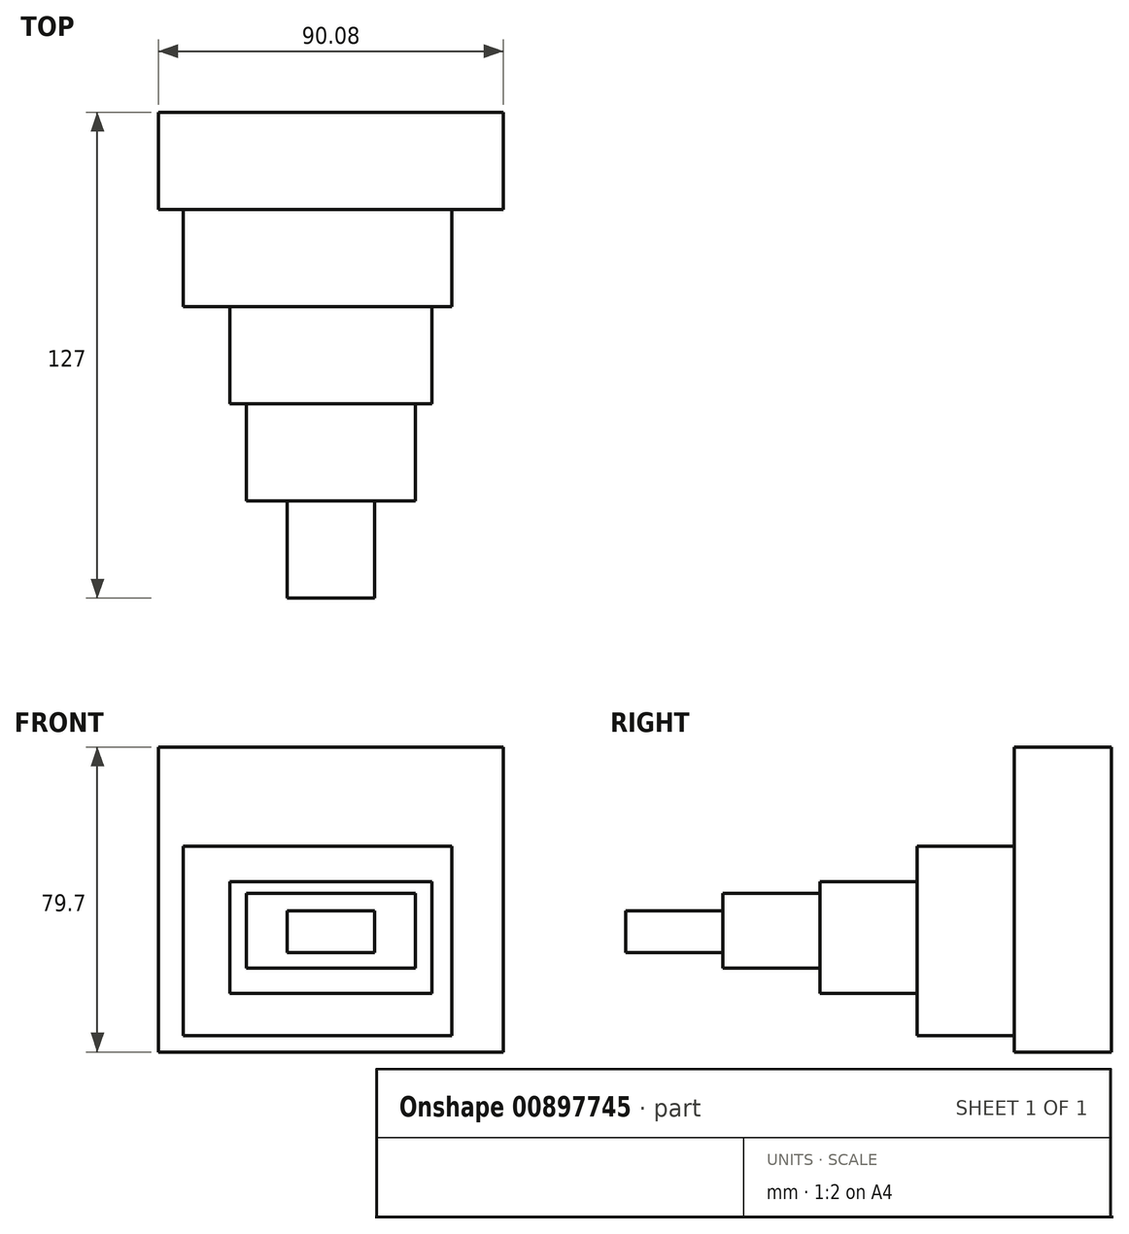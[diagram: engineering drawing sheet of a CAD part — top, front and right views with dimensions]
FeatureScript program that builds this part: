
annotation { "Feature Type Name" : "Feature", "Feature Type Description" : "" }
export const myFeature = defineFeature(function(context is Context, id is Id, definition is map)
    precondition{}
    {
        {
            var Q0;
            Q0=qCreatedBy(makeId("Front.planeOp"),FACE);
            var sketch = newSketch(context, id + "F0", { "sketchPlane" : qUnion([Q0])});
            skLineSegment(sketch, "E0.bottom", {"start": v(45.04, -39.85) * mm, "end": v(-45.04, -39.85) * mm});
            skLineSegment(sketch, "E0.top", {"start": v(45.04, 39.85) * mm, "end": v(-45.04, 39.85) * mm});
            skLineSegment(sketch, "E0.left", {"start": v(45.04, -39.85) * mm, "end": v(45.04, 39.85) * mm});
            skLineSegment(sketch, "E0.right", {"start": v(-45.04, -39.85) * mm, "end": v(-45.04, 39.85) * mm});
            skPoint(sketch, "E0.middle", {"position": v(0, 0) * mm});
            skSolve(sketch);
        }
        {
            var Q0;
            Q0 = qSketchRegion(id + "F0", true);
            extrude(context, id + "F1", {"entities" : qUnion([Q0]), "depth" : 25.4 * mm, "offsetDistance" : 25.4 * mm});
        }
        {
            var Q0;
            Q0=makeQuery(id+"F1.opExtrude","CAP_FACE",FACE,{"disambiguationData":[OSD([sQuery(id+"F0.wireOp",EDGE,"E0.bottom"),sQuery(id+"F0.wireOp",EDGE,"E0.top"),sQuery(id+"F0.wireOp",EDGE,"E0.left"),sQuery(id+"F0.wireOp",EDGE,"E0.right")])],"isStart":false});
            var sketch = newSketch(context, id + "F2", { "sketchPlane" : qUnion([Q0])});
            skLineSegment(sketch, "E1.bottom", {"start": v(31.6, -35.58) * mm, "end": v(-38.63, -35.58) * mm});
            skLineSegment(sketch, "E1.top", {"start": v(31.6, 13.9) * mm, "end": v(-38.63, 13.9) * mm});
            skLineSegment(sketch, "E1.left", {"start": v(31.6, -35.58) * mm, "end": v(31.6, 13.9) * mm});
            skLineSegment(sketch, "E1.right", {"start": v(-38.63, -35.58) * mm, "end": v(-38.63, 13.9) * mm});
            skPoint(sketch, "E1.middle", {"position": v(-3.51, -10.84) * mm});
            skSolve(sketch);
        }
        {
            var Q0;
            Q0 = qSketchRegion(id + "F2", true);
            extrude(context, id + "F3", {"entities" : qUnion([Q0]), "operationType" : NewBodyOperationType.ADD, "depth" : 25.4 * mm, "offsetDistance" : 25.4 * mm});
        }
        {
            var Q0;
            Q0=makeQuery(id+"F3.opExtrude","CAP_FACE",FACE,{"disambiguationData":[OSD([sQuery(id+"F2.wireOp",EDGE,"E1.bottom"),sQuery(id+"F2.wireOp",EDGE,"E1.top"),sQuery(id+"F2.wireOp",EDGE,"E1.left"),sQuery(id+"F2.wireOp",EDGE,"E1.right")])],"isStart":false});
            var sketch = newSketch(context, id + "F4", { "sketchPlane" : qUnion([Q0])});
            skLineSegment(sketch, "E2.bottom", {"start": v(26.42, -24.58) * mm, "end": v(-26.42, -24.58) * mm});
            skLineSegment(sketch, "E2.top", {"start": v(26.42, 4.73) * mm, "end": v(-26.42, 4.73) * mm});
            skLineSegment(sketch, "E2.left", {"start": v(26.42, -24.58) * mm, "end": v(26.42, 4.73) * mm});
            skLineSegment(sketch, "E2.right", {"start": v(-26.42, -24.58) * mm, "end": v(-26.42, 4.73) * mm});
            skPoint(sketch, "E2.middle", {"position": v(0, -9.92) * mm});
            skSolve(sketch);
        }
        {
            var Q0;
            Q0 = qSketchRegion(id + "F4", true);
            extrude(context, id + "F5", {"entities" : qUnion([Q0]), "operationType" : NewBodyOperationType.ADD, "depth" : 25.4 * mm, "offsetDistance" : 25.4 * mm});
        }
        {
            var Q0;
            Q0=makeQuery(id+"F5.opExtrude","CAP_FACE",FACE,{"disambiguationData":[OSD([sQuery(id+"F4.wireOp",EDGE,"E2.bottom"),sQuery(id+"F4.wireOp",EDGE,"E2.top"),sQuery(id+"F4.wireOp",EDGE,"E2.left"),sQuery(id+"F4.wireOp",EDGE,"E2.right")])],"isStart":false});
            var sketch = newSketch(context, id + "F6", { "sketchPlane" : qUnion([Q0])});
            skLineSegment(sketch, "E3.bottom", {"start": v(22.14, -17.86) * mm, "end": v(-22.14, -17.86) * mm});
            skLineSegment(sketch, "E3.top", {"start": v(22.14, 1.68) * mm, "end": v(-22.14, 1.68) * mm});
            skLineSegment(sketch, "E3.left", {"start": v(22.14, -17.86) * mm, "end": v(22.14, 1.68) * mm});
            skLineSegment(sketch, "E3.right", {"start": v(-22.14, -17.86) * mm, "end": v(-22.14, 1.68) * mm});
            skPoint(sketch, "E3.middle", {"position": v(0, -8.1) * mm});
            skSolve(sketch);
        }
        {
            var Q0;
            Q0 = qSketchRegion(id + "F6", true);
            extrude(context, id + "F7", {"entities" : qUnion([Q0]), "operationType" : NewBodyOperationType.ADD, "depth" : 25.4 * mm, "offsetDistance" : 25.4 * mm});
        }
        {
            var Q0;
            Q0=makeQuery(id+"F7.opExtrude","CAP_FACE",FACE,{"disambiguationData":[OSD([sQuery(id+"F6.wireOp",EDGE,"E3.bottom"),sQuery(id+"F6.wireOp",EDGE,"E3.top"),sQuery(id+"F6.wireOp",EDGE,"E3.left"),sQuery(id+"F6.wireOp",EDGE,"E3.right")])],"isStart":false});
            var sketch = newSketch(context, id + "F8", { "sketchPlane" : qUnion([Q0])});
            skLineSegment(sketch, "E4.bottom", {"start": v(11.45, -13.9) * mm, "end": v(-11.45, -13.9) * mm});
            skLineSegment(sketch, "E4.top", {"start": v(11.45, -2.9) * mm, "end": v(-11.45, -2.9) * mm});
            skLineSegment(sketch, "E4.left", {"start": v(11.45, -13.9) * mm, "end": v(11.45, -2.9) * mm});
            skLineSegment(sketch, "E4.right", {"start": v(-11.45, -13.9) * mm, "end": v(-11.45, -2.9) * mm});
            skPoint(sketch, "E4.middle", {"position": v(0, -8.4) * mm});
            skSolve(sketch);
        }
        {
            var Q0;
            Q0 = qSketchRegion(id + "F8", true);
            extrude(context, id + "F9", {"entities" : qUnion([Q0]), "operationType" : NewBodyOperationType.ADD, "depth" : 25.4 * mm, "offsetDistance" : 25.4 * mm});
        }
    });
